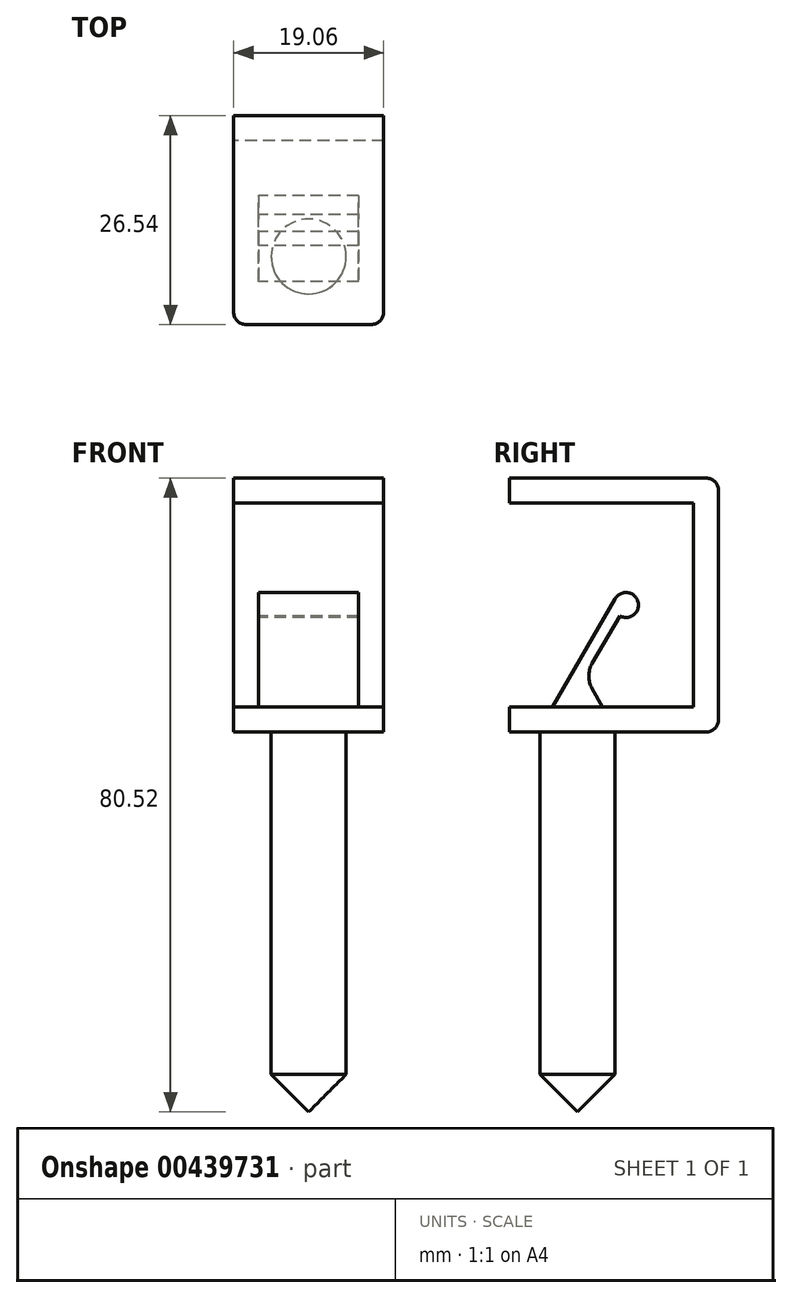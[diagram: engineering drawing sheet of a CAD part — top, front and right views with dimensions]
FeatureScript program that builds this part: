
annotation { "Feature Type Name" : "Feature", "Feature Type Description" : "" }
export const myFeature = defineFeature(function(context is Context, id is Id, definition is map)
    precondition{}
    {
        {
            var Q0;
            Q0=qCreatedBy(makeId("Right.planeOp"),FACE);
            var sketch = newSketch(context, id + "F0", { "sketchPlane" : qUnion([Q0])});
            skLineSegment(sketch, "E0.bottom", {"start": v(0, 0) * mm, "end": v(26.54, 0) * mm});
            skLineSegment(sketch, "E0.top", {"start": v(0, 3.18) * mm, "end": v(23.37, 3.18) * mm});
            skLineSegment(sketch, "E0.left", {"start": v(0, 0) * mm, "end": v(0, 3.18) * mm});
            skLineSegment(sketch, "E1.bottom", {"start": v(0, 32.26) * mm, "end": v(26.54, 32.26) * mm});
            skLineSegment(sketch, "E1.top", {"start": v(0, 29.08) * mm, "end": v(23.37, 29.08) * mm});
            skLineSegment(sketch, "E2", {"start": v(0, 32.26) * mm, "end": v(0, 29.08) * mm});
            skLineSegment(sketch, "E3", {"start": v(23.37, 3.18) * mm, "end": v(23.37, 29.08) * mm});
            skLineSegment(sketch, "E4", {"start": v(26.54, 0) * mm, "end": v(26.54, 32.26) * mm});
            skLineSegment(sketch, "E5", {"start": v(23.37, 29.08) * mm, "end": v(26.54, 29.08) * mm, "construction": true});
            skLineSegment(sketch, "E6", {"start": v(3.18, 21.78) * mm, "end": v(15.37, 21.78) * mm, "construction": true});
            skSolve(sketch);
        }
        {
            var Q0;
            Q0=qSketchRegion(id+"F0",true);
            extrude(context, id + "F1", {"entities" : qUnion([Q0]), "endBound" : BoundingType.SYMMETRIC, "depth" : 19.05 * mm});
        }
        {
            var Q0;
            Q0=makeQuery(id+"F1.opExtrude","CAP_EDGE",EDGE,{"disambiguationData":[OSD([sQuery(id+"F0.wireOp",EDGE,"E2")])],"isStart":false});
            var Q1;
            Q1=makeQuery(id+"F1.opExtrude","CAP_EDGE",EDGE,{"disambiguationData":[OSD([sQuery(id+"F0.wireOp",EDGE,"E2")])],"isStart":true});
            var Q2;
            Q2=makeQuery(id+"F1.opExtrude","CAP_EDGE",EDGE,{"disambiguationData":[OSD([sQuery(id+"F0.wireOp",EDGE,"E0.left")])],"isStart":true});
            var Q3;
            Q3=makeQuery(id+"F1.opExtrude","CAP_EDGE",EDGE,{"disambiguationData":[OSD([sQuery(id+"F0.wireOp",EDGE,"E0.left")])],"isStart":false});
            var Q4;
            Q4=makeQuery(id+"F1.opExtrude","SWEPT_EDGE",EDGE,{"disambiguationData":[OSD([sQuery(id+"F0.wireOp",EDGE,"E1.bottom"),sQuery(id+"F0.wireOp",EDGE,"E4")])]});
            var Q5;
            Q5=makeQuery(id+"F1.opExtrude","SWEPT_EDGE",EDGE,{"disambiguationData":[OSD([sQuery(id+"F0.wireOp",EDGE,"E0.bottom"),sQuery(id+"F0.wireOp",EDGE,"E4")])]});
            fillet(context, id + "F2", {"entities" : qUnion([Q0, Q1, Q2, Q3, Q4, Q5]), "radius" : 1.59 * mm, "tangentPropagation" : true, "allowEdgeOverflow" : false});
        }
        {
            var Q0;
            Q0=qCreatedBy(makeId("Right.planeOp"),FACE);
            var sketch = newSketch(context, id + "F3", { "sketchPlane" : qUnion([Q0])});
            skLineSegment(sketch, "E7", {"start": v(5.47, 3.17) * mm, "end": v(13.4, 16.92) * mm});
            skArc(sketch, "E8", {"start": v(13.99, 14.75) * mm, "mid": v(16.31, 16.54) * mm, "end": v(13.4, 16.92) * mm});
            skLineSegment(sketch, "E9", {"start": v(10.48, 5.5) * mm, "end": v(11.82, 3.17) * mm});
            skLineSegment(sketch, "E10", {"start": v(11.82, 3.18) * mm, "end": v(5.47, 3.18) * mm});
            skPoint(sketch, "E11", {"position": v(16.37, 16.13) * mm});
            skArc(sketch, "E12", {"start": v(10.48, 8.67) * mm, "mid": v(10.05, 7.09) * mm, "end": v(10.48, 5.5) * mm});
            skLineSegment(sketch, "E13", {"start": v(10.48, 8.67) * mm, "end": v(13.99, 14.75) * mm});
            skPoint(sketch, "E14", {"position": v(23.37, 16.13) * mm});
            skSolve(sketch);
        }
        {
            var Q0;
            Q0 = qSketchRegion(id + "F3", true);
            extrude(context, id + "F4", {"entities" : qUnion([Q0]), "operationType" : NewBodyOperationType.ADD, "endBound" : BoundingType.SYMMETRIC, "depth" : 12.7 * mm});
        }
        {
            var Q0;
            Q0=qCreatedBy(makeId("Right.planeOp"),FACE);
            var sketch = newSketch(context, id + "F5", { "sketchPlane" : qUnion([Q0])});
            skLineSegment(sketch, "E15", {"start": v(3.88, 0) * mm, "end": v(3.88, -43.5) * mm});
            skLineSegment(sketch, "E16", {"start": v(3.88, -43.5) * mm, "end": v(8.64, -48.26) * mm});
            skLineSegment(sketch, "E17", {"start": v(8.64, -48.26) * mm, "end": v(8.64, 0) * mm});
            skLineSegment(sketch, "E18", {"start": v(8.64, 0) * mm, "end": v(3.88, 0) * mm});
            skPoint(sketch, "E19", {"position": v(8.64, 3.18) * mm});
            skSolve(sketch);
        }
        {
            var Q0;
            Q0=makeQuery(id+"F5.imprint","IMPRINT",FACE,{"disambiguationData":[TD([[makeQuery(id+"F5.imprint","IMPRINT",EDGE,{"derivedFrom":sQuery(id+"F5.wireOp",EDGE,"E15")}),1.0]])]});
            var Q1;
            Q1=sQuery(id+"F5.wireOp",EDGE,"E17");
            revolve(context, id + "F6", {"operationType" : NewBodyOperationType.ADD, "entities" : qUnion([Q0]), "axis" : qUnion([Q1]), "revolveType" : RevolveType.FULL});
        }
    });
